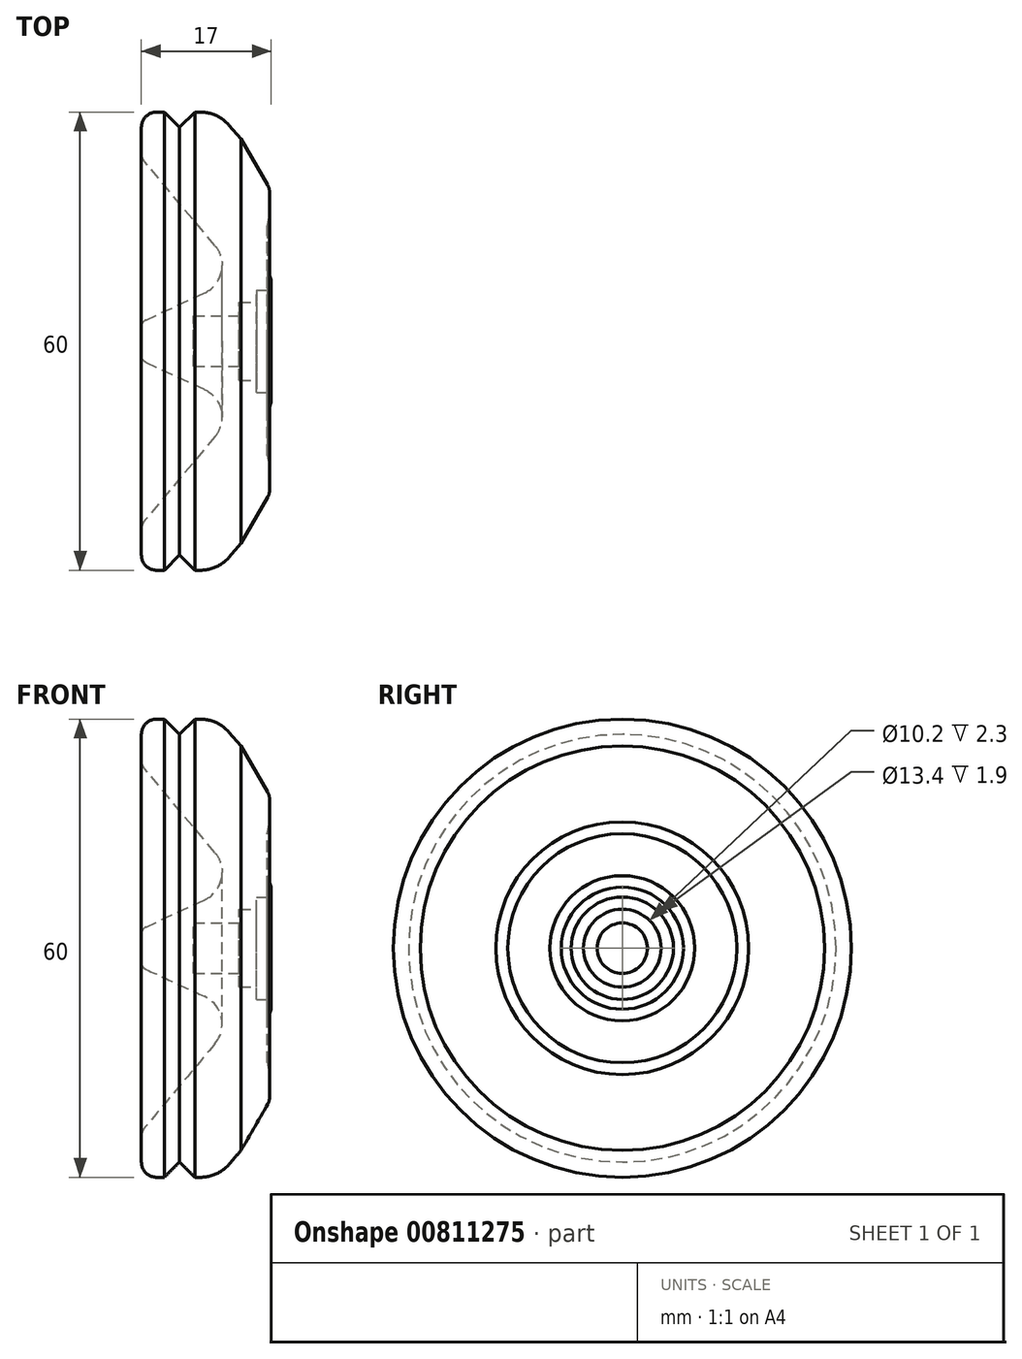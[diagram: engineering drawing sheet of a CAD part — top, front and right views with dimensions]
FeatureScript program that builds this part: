
annotation { "Feature Type Name" : "Feature", "Feature Type Description" : "" }
export const myFeature = defineFeature(function(context is Context, id is Id, definition is map)
    precondition{}
    {
        {
            var Q0;
            Q0=qCreatedBy(makeId("Front.planeOp"),FACE);
            var sketch = newSketch(context, id + "F0", { "sketchPlane" : qUnion([Q0])});
            skLineSegment(sketch, "E0", {"start": v(2, 30) * mm, "end": v(3, 30) * mm});
            skLineSegment(sketch, "E1", {"start": v(3, 30) * mm, "end": v(5, 28) * mm});
            skLineSegment(sketch, "E2", {"start": v(5, 28) * mm, "end": v(7, 30) * mm});
            skLineSegment(sketch, "E3", {"start": v(15.1, 5.1) * mm, "end": v(12.8, 5.1) * mm});
            skLineSegment(sketch, "E4", {"start": v(12.8, 5.1) * mm, "end": v(12.8, 3.3) * mm});
            skLineSegment(sketch, "E5", {"start": v(12.8, 3.3) * mm, "end": v(6.8, 3.3) * mm});
            skLineSegment(sketch, "E6", {"start": v(6.8, 3.3) * mm, "end": v(6.8, 0) * mm});
            skLineSegment(sketch, "E7", {"start": v(6.8, 0) * mm, "end": v(0, 0) * mm});
            skPoint(sketch, "E8.visualSharp", {"position": v(0, 30) * mm});
            skLineSegment(sketch, "E9", {"start": v(15.1, 5.1) * mm, "end": v(15.1, 6.7) * mm});
            skLineSegment(sketch, "E10", {"start": v(15.1, 6.7) * mm, "end": v(17, 6.7) * mm});
            skLineSegment(sketch, "E11", {"start": v(17, 6.7) * mm, "end": v(17, 8) * mm});
            skLineSegment(sketch, "E12", {"start": v(16.5, 15) * mm, "end": v(16.5, 9.5) * mm});
            skLineSegment(sketch, "E13", {"start": v(16.5, 9.5) * mm, "end": v(17, 8) * mm});
            skLineSegment(sketch, "E14", {"start": v(0, 1.86) * mm, "end": v(0, 0) * mm});
            skLineSegment(sketch, "E15", {"start": v(16.8, 16.55) * mm, "end": v(16.5, 15) * mm});
            skPoint(sketch, "E16.visualSharp", {"position": v(16.8, 20) * mm});
            skPoint(sketch, "E17.visualSharp", {"position": v(0, 24) * mm});
            skLineSegment(sketch, "E18", {"start": v(7, 30) * mm, "end": v(7.72, 30) * mm});
            skLineSegment(sketch, "E19", {"start": v(11.5, 28.28) * mm, "end": v(13.06, 26.48) * mm});
            skLineSegment(sketch, "E20", {"start": v(13.06, 26.48) * mm, "end": v(16.53, 20.46) * mm});
            skLineSegment(sketch, "E21", {"start": v(16.8, 16.55) * mm, "end": v(16.8, 19.46) * mm});
            skPoint(sketch, "E22.visualSharp", {"position": v(10, 30) * mm});
            skArc(sketch, "E22.filletArc", {"start": v(11.5, 28.28) * mm, "mid": v(9.8, 29.55) * mm, "end": v(7.72, 30) * mm});
            skArc(sketch, "E23.filletArc", {"start": v(16.8, 19.46) * mm, "mid": v(16.73, 19.98) * mm, "end": v(16.53, 20.46) * mm});
            skLineSegment(sketch, "E24", {"start": v(0, 28) * mm, "end": v(0, 24.73) * mm});
            skPoint(sketch, "E25.visualSharp", {"position": v(0, 2.5) * mm});
            skPoint(sketch, "E26.visualSharp", {"position": v(13, 8.5) * mm});
            skLineSegment(sketch, "E27", {"start": v(9.64, 12.5) * mm, "end": v(0.47, 23.44) * mm});
            skLineSegment(sketch, "E28", {"start": v(0.58, 2.77) * mm, "end": v(8.25, 6.3) * mm});
            skArc(sketch, "E29.filletArc", {"start": v(0, 24.73) * mm, "mid": v(0.12, 24.04) * mm, "end": v(0.47, 23.44) * mm});
            skArc(sketch, "E30.filletArc", {"start": v(2, 30) * mm, "mid": v(0.59, 29.41) * mm, "end": v(0, 28) * mm});
            skArc(sketch, "E31.filletArc", {"start": v(8.25, 6.3) * mm, "mid": v(10.48, 9.07) * mm, "end": v(9.64, 12.5) * mm});
            skArc(sketch, "E32.filletArc", {"start": v(0.58, 2.77) * mm, "mid": v(0.16, 2.4) * mm, "end": v(0, 1.86) * mm});
            skSolve(sketch);
        }
        {
            var Q0;
            Q0=makeQuery(id+"F0.imprint","IMPRINT",FACE,{"disambiguationData":[TD([[makeQuery(id+"F0.imprint","IMPRINT",EDGE,{"derivedFrom":sQuery(id+"F0.wireOp",EDGE,"E0")}),-1.0]])]});
            var Q1;
            Q1=sQuery(id+"F0.wireOp",EDGE,"E7");
            revolve(context, id + "F1", {"surfaceOperationType" : NewSurfaceOperationType.NEW, "entities" : qUnion([Q0]), "axis" : qUnion([Q1]), "revolveType" : RevolveType.FULL});
        }
    });
